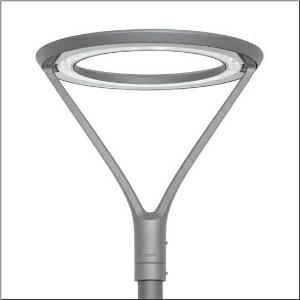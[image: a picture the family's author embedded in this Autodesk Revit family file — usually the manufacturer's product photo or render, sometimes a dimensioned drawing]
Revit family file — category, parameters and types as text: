
# Revit family: dl_r__20_led___st1_2a_5xa51283na008p_9dd8
name_source: partatom
category: Lighting Fixtures
units: mm (PartAtom-declared; Revit-internal decimal feet)

## family parameters
Cut with Voids When Loaded = No
Host = Face
Light Source = No
Part Type = Normal
Room Calculation Point = No
Round Connector Dimension = Use Diameter
Shared = No

## types (1)
- --- (1 x LED 4000K / CRI = 80 (unbekannt), 5300 lm, 4000K)
    Apparent Load = 53 VA
    CIE Flux Codes = 31 69 96 100 100
    Color Rendering = 80
    Color Temperature = 4000K
    Default Elevation = 1800 mm
    Description = DL® 20 LED, mast luminaire, primary light control with reflector, highly specular, primary optical cover: cover, of toughened safety glass of clear glass with excellent transmission level, light distribution: ST1.2a, light emission: direct distribution, primary light characteristic: asymmetric, installation type: post-top, LED High Power LED, rated luminous flux: 5.300 lm, light colour: 840, colour temperature: 4000K, control gear: ECG Plus, control: overheat protection, power reduction, digital communication interface, constant luminous flux control, time-dependent luminous flux control, flexible luminous flux parameterisation, electronic power reduction, mains connection: 220..240V, 50/60Hz, connection cable pre-assembled, cable length: 5 m, start of lifetime: 53 W, end of lifetime: 54 W, reduction: 24 W, luminaire housing, upper part, of cast aluminium, powder-coated, Siteco® metallic grey (DB 702S), diameter: 690 mm, height: 690mm, spigot size: 76mm (post-top), luminaire housing, of cast aluminium, powder-coated, Siteco® metallic grey (DB 702S), protection rating (complete): IP66, insulation class (complete): insulation class II (safety insulation), certification: CE, ENEC, VDE, impact resistance: IK08, permissible ambient temperature for indoor applications: -25..+30°C, standard-compliant lighting for roads and squares, packaging unit: 1 piece

Light Distribution: ST1.2a
    Height = 690 mm
    Lamp = 1 x LED 4000K / CRI >= 80 (unbekannt)
    Lamp Light Flux = 5300 lm
    Lamp count = 1
    Length = 690 mm
    Luminous efficacy = 101 lm/W
    Manufacturer = Siteco
    ModVariant = No
    Model = 5XA51283NA008P
    Number of Poles = 1
    OnlyDefault = Yes
    Power Factor = 1
    Product Name = DL® 20 LED | ST1.2a
    Product group = mast luminaire | pylon top
    ProductGroupID = 6100
    Protection Class = Protection class II
    Protection Degree = IP 66
    RLX_Detail_Level = 1
    RlxData = <blob elided: 206733 chars, md5=127babb0>
    Socket = socket
    Standby Power = 0 W
    System Light Flux = 5300 lm
    System Power = 53 W
    Type Comments = factory setting: luminous flux: 100 % | dim-lin: 254 | 683 mA
    Type Image = l_1006001.jpg
    URL = http://relux.com
    VarID = @adj_141349
    Voltage = 0 V
    Weight = 0.00 kg
    Width = 0 mm  [stored 0 ft]

note: [stored X ft] marks values corroborated as IEEE doubles in the binary element streams (Revit-internal decimal feet)

## geometry (parser evidence)
native form markers: Blend x4, Sweep x10
no freeform markers — native parametric forms only
